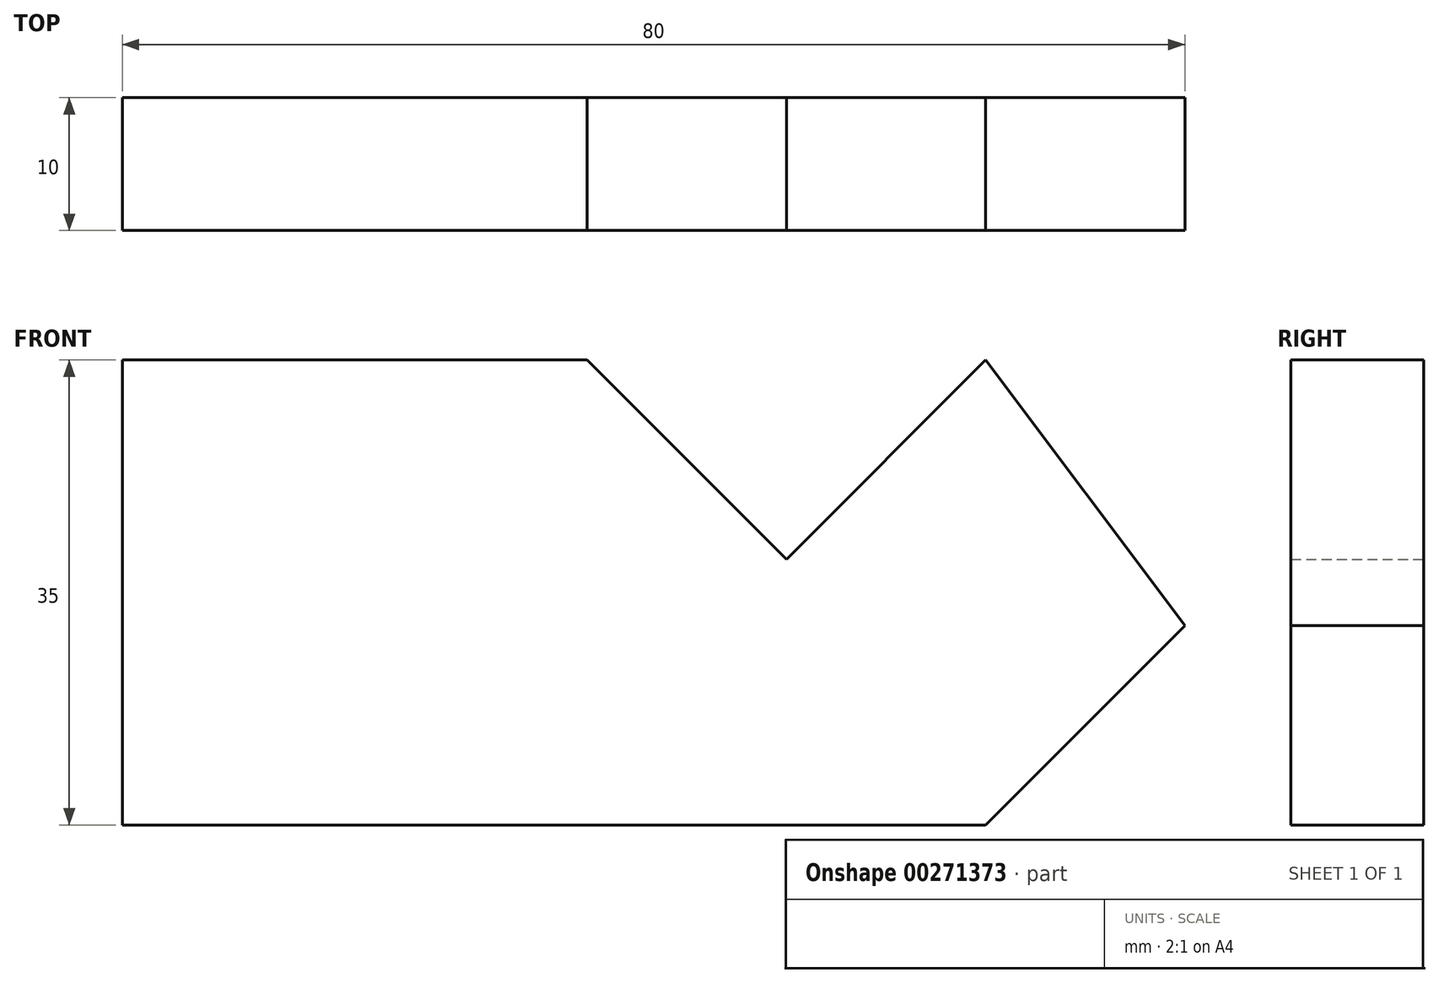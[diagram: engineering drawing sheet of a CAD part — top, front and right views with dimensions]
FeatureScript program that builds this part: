
annotation { "Feature Type Name" : "Feature", "Feature Type Description" : "" }
export const myFeature = defineFeature(function(context is Context, id is Id, definition is map)
    precondition{}
    {
        {
            var Q0;
            Q0=qCreatedBy(makeId("Front.planeOp"),FACE);
            var sketch = newSketch(context, id + "F0", { "sketchPlane" : qUnion([Q0])});
            skLineSegment(sketch, "E0", {"start": v(0, 0) * mm, "end": v(0, 35) * mm});
            skLineSegment(sketch, "E1", {"start": v(0, 0) * mm, "end": v(65, 0) * mm});
            skLineSegment(sketch, "E2", {"start": v(65, 0) * mm, "end": v(80, 15) * mm});
            skLineSegment(sketch, "E3", {"start": v(0, 35) * mm, "end": v(35, 35) * mm});
            skLineSegment(sketch, "E4", {"start": v(35, 35) * mm, "end": v(50, 20) * mm});
            skLineSegment(sketch, "E5", {"start": v(50, 20) * mm, "end": v(65, 35) * mm});
            skLineSegment(sketch, "E6", {"start": v(65, 35) * mm, "end": v(80, 15) * mm});
            skSolve(sketch);
        }
        {
            var Q0;
            Q0=makeQuery(id+"F0.imprint","IMPRINT",FACE,{"disambiguationData":[TD([[makeQuery(id+"F0.imprint","IMPRINT",EDGE,{"derivedFrom":sQuery(id+"F0.wireOp",EDGE,"E0")}),-1.0]])]});
            extrude(context, id + "F1", {"entities" : qUnion([Q0]), "depth" : 10 * mm});
        }
    });
